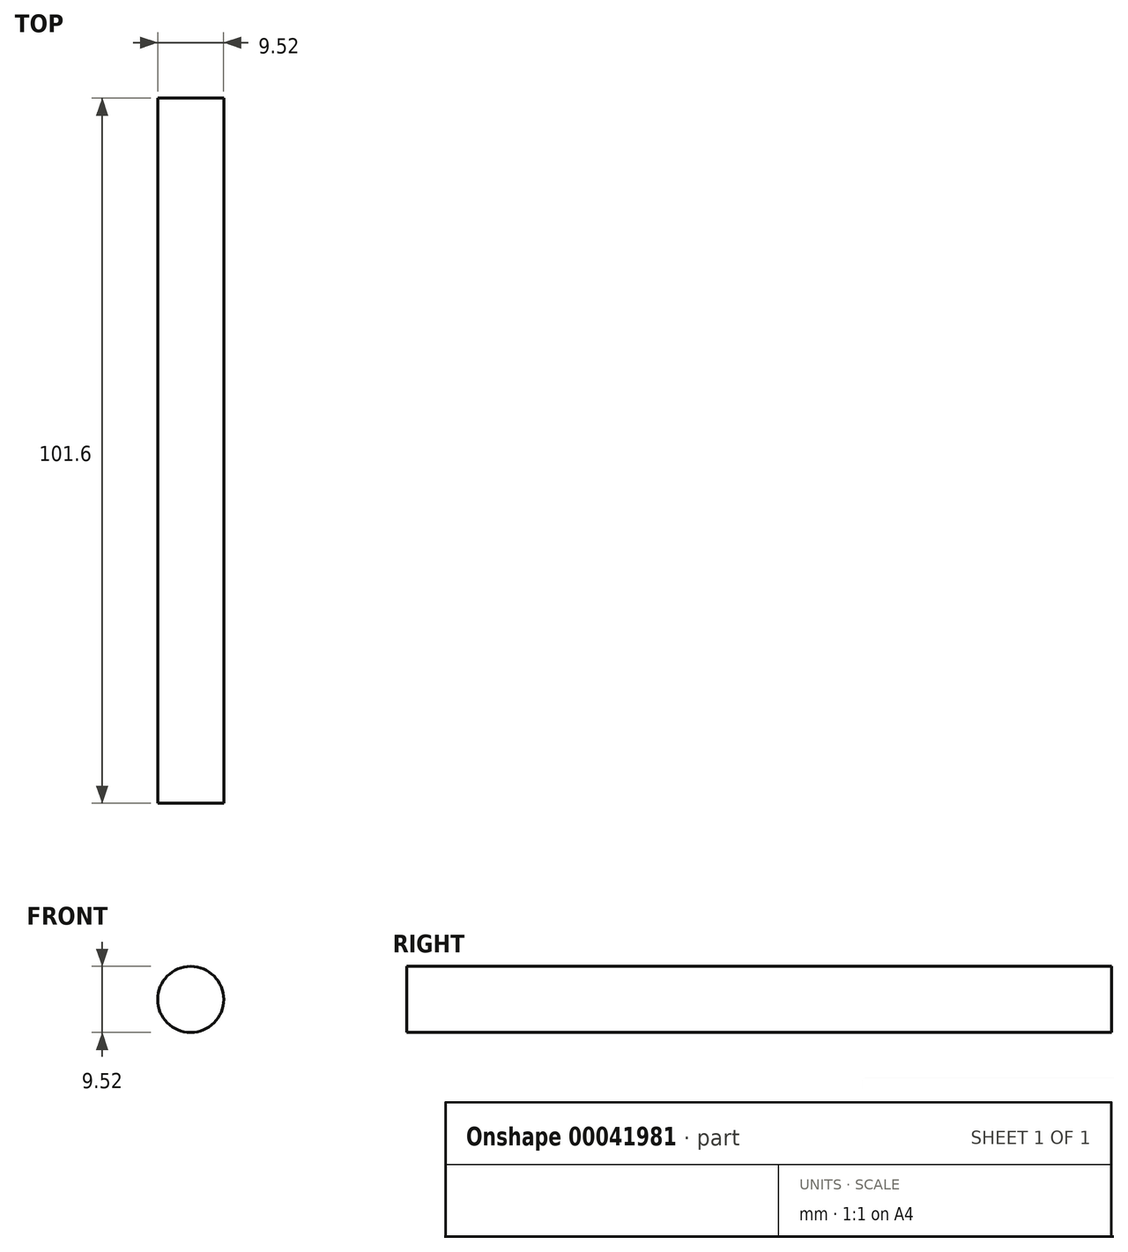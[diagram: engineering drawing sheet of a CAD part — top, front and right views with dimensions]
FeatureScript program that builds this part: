
annotation { "Feature Type Name" : "Feature", "Feature Type Description" : "" }
export const myFeature = defineFeature(function(context is Context, id is Id, definition is map)
    precondition{}
    {
        {
            var Q0;
            Q0=qCreatedBy(makeId("Front.planeOp"),FACE);
            var sketch = newSketch(context, id + "F0", { "sketchPlane" : qUnion([Q0])});
            skCircle(sketch, "E0", {"center": v(0, 0) * mm, "radius": 4.76 * mm});
            skSolve(sketch);
        }
        {
            var Q0;
            Q0=qSketchRegion(id+"F0",true);
            extrude(context, id + "F1", {"entities" : qUnion([Q0]), "depth" : 101.6 * mm});
        }
    });
